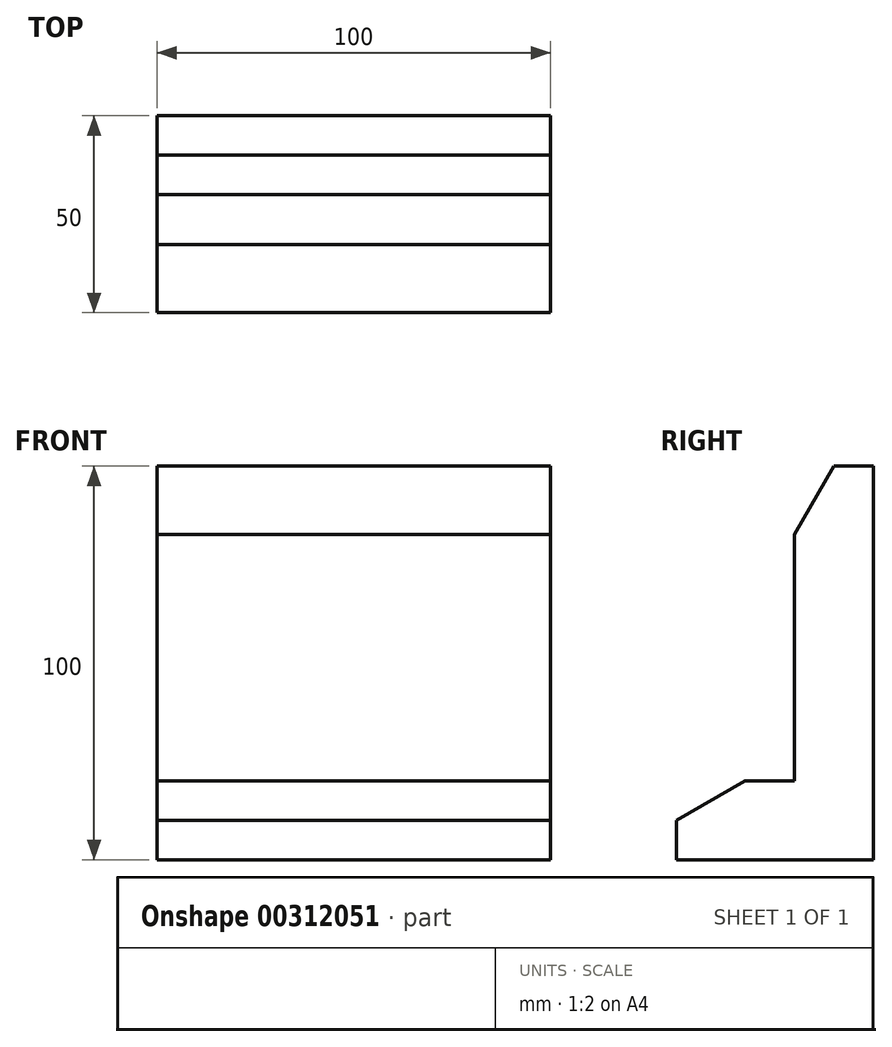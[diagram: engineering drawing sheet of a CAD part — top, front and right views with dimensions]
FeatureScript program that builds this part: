
annotation { "Feature Type Name" : "Feature", "Feature Type Description" : "" }
export const myFeature = defineFeature(function(context is Context, id is Id, definition is map)
    precondition{}
    {
        {
            var Q0;
            Q0=qCreatedBy(makeId("Front.planeOp"),FACE);
            var sketch = newSketch(context, id + "F0", { "sketchPlane" : qUnion([Q0])});
            skLineSegment(sketch, "E0.bottom", {"start": v(-50, 50) * mm, "end": v(50, 50) * mm});
            skLineSegment(sketch, "E0.top", {"start": v(-50, -50) * mm, "end": v(50, -50) * mm});
            skLineSegment(sketch, "E0.left", {"start": v(-50, 50) * mm, "end": v(-50, -50) * mm});
            skLineSegment(sketch, "E0.right", {"start": v(50, 50) * mm, "end": v(50, -50) * mm});
            skPoint(sketch, "E0.middle", {"position": v(0, 0) * mm});
            skSolve(sketch);
        }
        {
            var Q0;
            Q0 = qSketchRegion(id + "F0", true);
            extrude(context, id + "F1", {"entities" : qUnion([Q0]), "depth" : 50 * mm});
        }
        {
            var Q0;
            Q0=makeQuery(id+"F1.opExtrude","SWEPT_FACE",FACE,{"disambiguationData":[OSD([sQuery(id+"F0.wireOp",EDGE,"E0.right")])]});
            var sketch = newSketch(context, id + "F2", { "sketchPlane" : qUnion([Q0])});
            skLineSegment(sketch, "E1.bottom", {"start": v(-20, -30) * mm, "end": v(-80, -30) * mm});
            skLineSegment(sketch, "E1.top", {"start": v(-20, 130) * mm, "end": v(-80, 130) * mm});
            skLineSegment(sketch, "E1.left", {"start": v(-20, -30) * mm, "end": v(-20, 130) * mm});
            skLineSegment(sketch, "E1.right", {"start": v(-80, -30) * mm, "end": v(-80, 130) * mm});
            skPoint(sketch, "E1.middle", {"position": v(-50, 50) * mm});
            skLineSegment(sketch, "E2", {"start": v(-20, 32.68) * mm, "end": v(-10, 50) * mm});
            skLineSegment(sketch, "E3", {"start": v(-50, -40) * mm, "end": v(-32.68, -30) * mm});
            skSolve(sketch);
        }
        {
            var Q0;
            Q0 = qSketchRegion(id + "F2", true);
            var Q1;
            {var subQ0=sQuery(id+"F2.wireOp",EDGE,"E2");Q1=makeQuery(id+"F2.imprint","IMPRINT",FACE,{"disambiguationData":[TD([[makeQuery(id+"F2.imprint","IMPRINT",EDGE,{"derivedFrom":subQ0}),1.0]])]});}
            var Q2;
            {var subQ0=sQuery(id+"F2.wireOp",EDGE,"E3");Q2=makeQuery(id+"F2.imprint","IMPRINT",FACE,{"disambiguationData":[TD([[makeQuery(id+"F2.imprint","IMPRINT",EDGE,{"derivedFrom":subQ0}),1.0]])]});}
            extrude(context, id + "F3", {"entities" : qUnion([Q0, Q1, Q2]), "operationType" : NewBodyOperationType.REMOVE, "endBound" : BoundingType.THROUGH_ALL, "oppositeDirection" : true, "depth" : 25 * mm});
        }
    });
